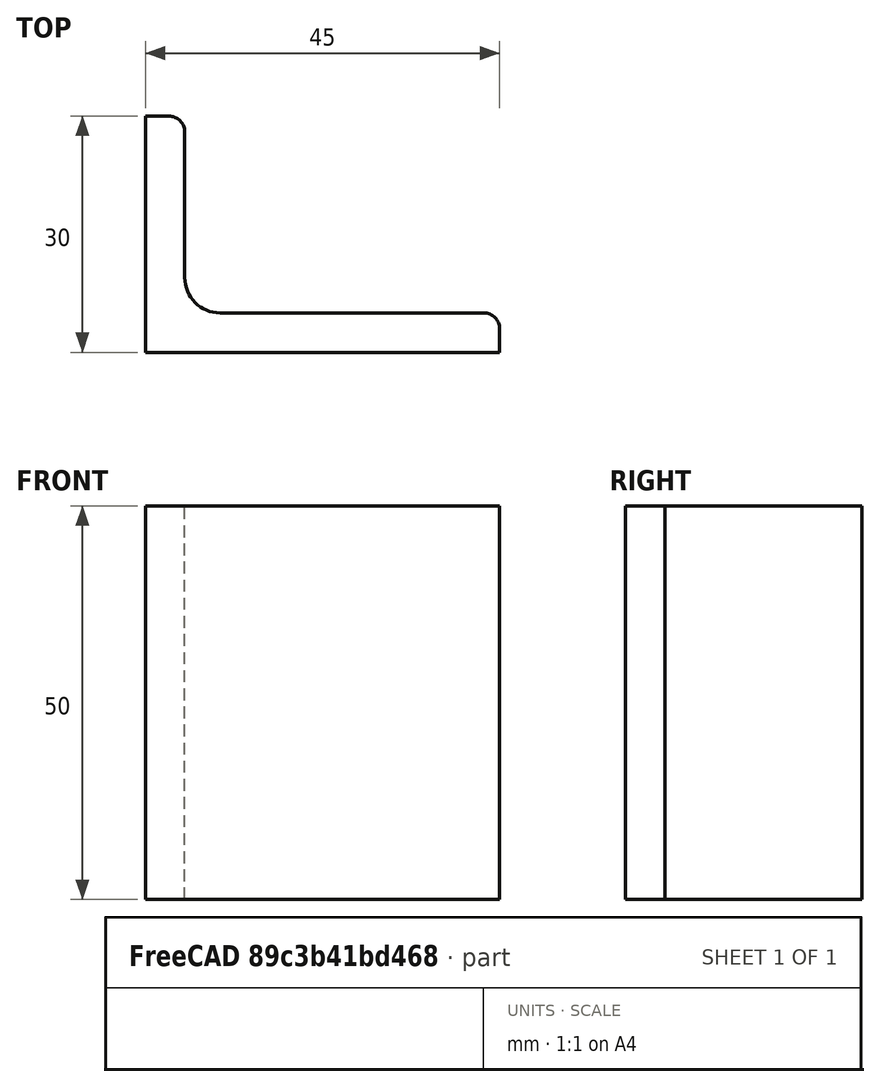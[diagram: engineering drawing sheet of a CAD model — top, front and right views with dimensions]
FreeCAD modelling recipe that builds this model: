
FCSTD DOCUMENT  (FreeCAD 0.15R4671 (Git))
Label: Angle Bar 45x30x5 EN10056 S235JR
License: All rights reserved
LicenseURL: http://en.wikipedia.org/wiki/All_rights_reserved
objects: Sketcher::SketchObject×1, Part::Extrusion×1
note: 2 computed .brp shape members not serialized (recipe doc carries the construction recipe); baked Part::Feature solids carry a one-line shape summary decoded from their .brp

FEATURE [Sketcher::SketchObject] Sketch
  sketch-geometry (9):
    g0: LineSegment StartX=0 StartY=0 StartZ=0 EndX=45 EndY=0 EndZ=0
    g1: LineSegment StartX=45 StartY=0 StartZ=0 EndX=45 EndY=3 EndZ=0
    g2: LineSegment StartX=43 StartY=5 StartZ=0 EndX=9.5 EndY=5 EndZ=0
    g3: LineSegment StartX=0 StartY=0 StartZ=0 EndX=0 EndY=30 EndZ=0
    g4: LineSegment StartX=0 StartY=30 StartZ=0 EndX=3 EndY=30 EndZ=0
    g5: LineSegment StartX=5 StartY=28 StartZ=0 EndX=5 EndY=9.5 EndZ=0
    g6: ArcOfCircle CenterX=9.5 CenterY=9.5 CenterZ=0 NormalX=0 NormalY=0 NormalZ=1 Radius=4.5 StartAngle=3.14159 EndAngle=4.71239
    g7: ArcOfCircle CenterX=3 CenterY=28 CenterZ=0 NormalX=0 NormalY=0 NormalZ=1 Radius=2 StartAngle=0 EndAngle=1.5708
    g8: ArcOfCircle CenterX=43 CenterY=3 CenterZ=0 NormalX=0 NormalY=0 NormalZ=1 Radius=2 StartAngle=0 EndAngle=1.5708
  constraints (23):
    c: Coincident(g0,g-1)
    c: Horizontal(g0)
    c: Coincident(g1,g0)
    c: Vertical(g1)
    c: Horizontal(g2)
    c: Coincident(g3,g-1)
    c: Vertical(g3)
    c: Coincident(g4,g3)
    c: Horizontal(g4)
    c: Vertical(g5)
    c: Tangent(g5,g6) = -1.5708
    c: Tangent(g2,g6) = 1.5708
    c: Tangent(g4,g7) = 1.5708
    c: Tangent(g5,g7) = 1.5708
    c: Tangent(g2,g8) = -1.5708
    c: Tangent(g1,g8) = -1.5708
    c: DistanceX(g0) = 45
    c: DistanceY(g3) = 30
    c: DistanceY(g0,g2) = 5
    c: DistanceX(g3,g5) = 5
    c: Radius(g6) = 4.5
    c: Radius(g8) = 2
    c: Radius(g7) = 2
FEATURE [Part::Extrusion] Extrude  label="Angle Bar 45x30x5 EN10056 S235JR"
  Base = -> Sketch
  Dir = (0,0,50)
  Solid = true
